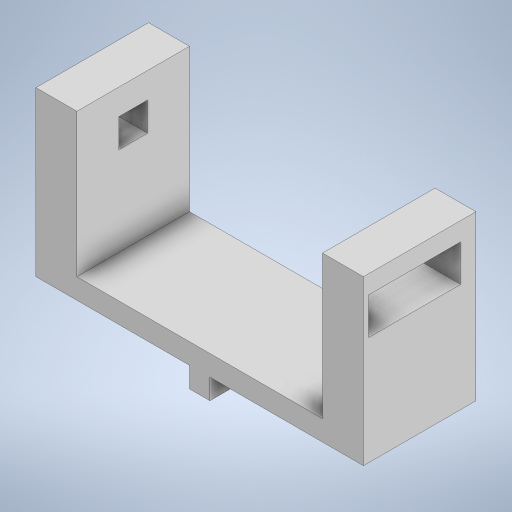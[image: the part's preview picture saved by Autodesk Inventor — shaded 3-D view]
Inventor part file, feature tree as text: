
AUTODESK INVENTOR PART (.ipt)
format: ipt  version: 2023 (Build 270158000, 158)  size: 253,952 bytes
history: native  units: mm
features: extrude x5, sketch x5, other x1
ambient origin geometry x8: Origin, YZ Plane, XZ Plane, XY Plane, X Axis, Y Axis, Z Axis, Center Point
bodies: Body1 (feature_tree)
feature tree (11):
  other  "Sólido1"
  extrude  "Extrusión1"  Depth=10.0mm
  extrude  "Extrusión2"  Depth=20.0mm
  extrude  "Extrusión3"  Depth=70.0mm TaperAngle=0.0deg
  extrude  "Extrusión4"  Depth=14.0mm
  extrude  "Extrusión5"  Depth=12.5mm
  sketch  "Boceto1"  dims[d0=160.0mm d1=10.0mm]
  sketch  "Boceto2"  dims[d2=55.0mm d3=0.0mm d4=20.0mm]
  sketch  "Boceto3"  dims[d5=20.0mm d6=70.0mm d7=0.0mm]
  sketch  "Boceto4"  dims[d10=14.0mm d11=14.0mm]
  sketch  "Boceto5"  dims[d12=20.5mm d13=12.5mm d14=70.0mm d15=0.0mm d17=10.0mm d18=10.0mm d19=0.0mm d20=45.0mm d21=18.0mm d22=9.0mm d23=7.5mm d24=30.0mm d25=0.0mm]
